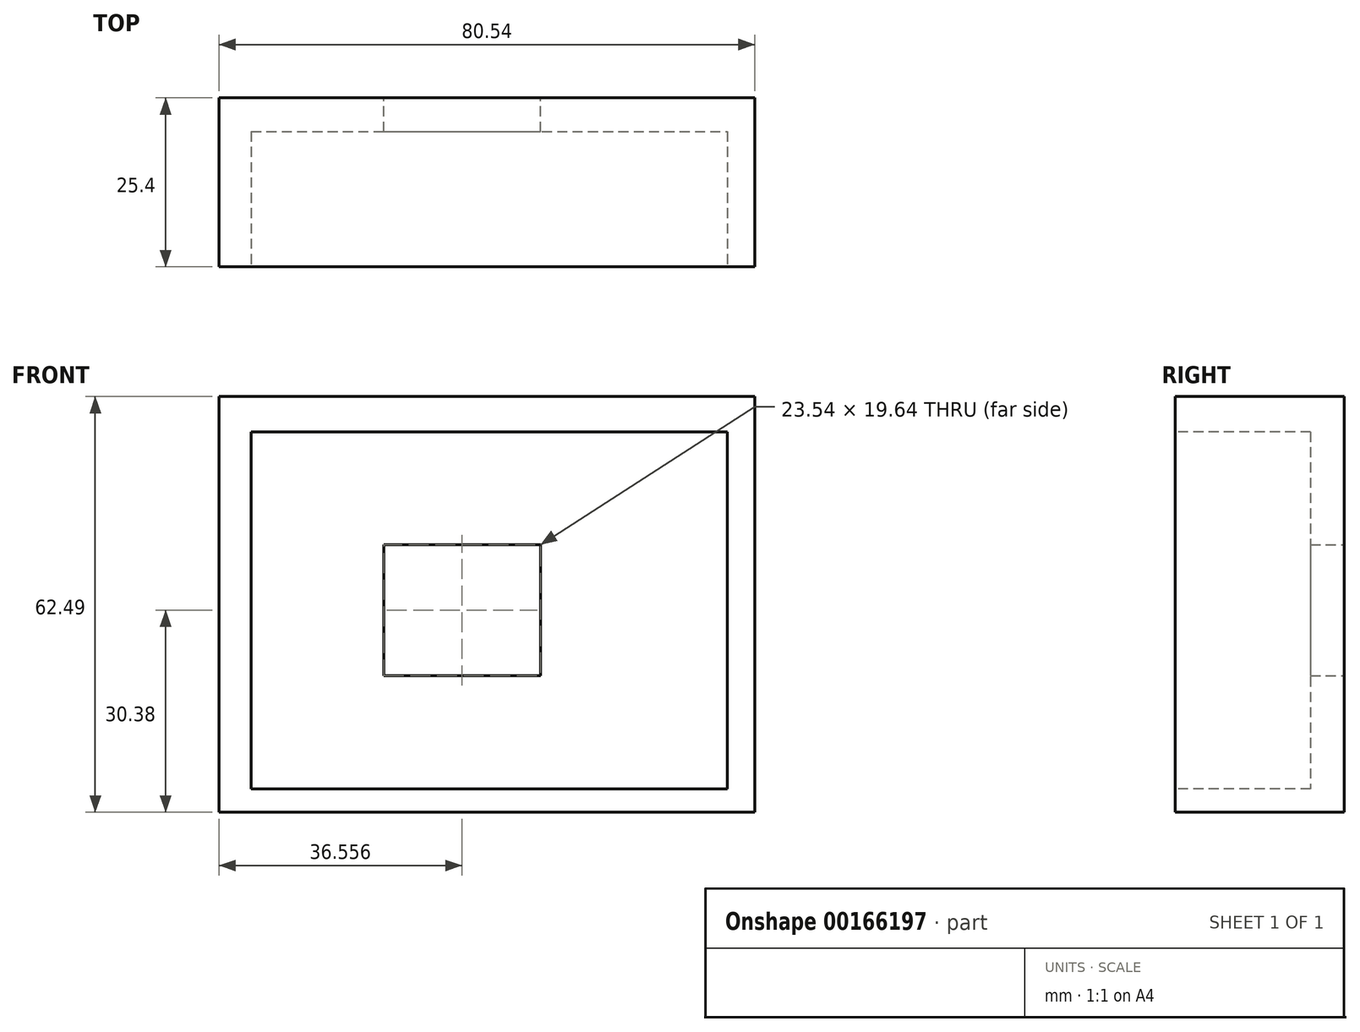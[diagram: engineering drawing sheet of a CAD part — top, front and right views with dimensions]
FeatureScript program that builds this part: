
annotation { "Feature Type Name" : "Feature", "Feature Type Description" : "" }
export const myFeature = defineFeature(function(context is Context, id is Id, definition is map)
    precondition{}
    {
        {
            var Q0;
            Q0=qCreatedBy(makeId("Front.planeOp"),FACE);
            var sketch = newSketch(context, id + "F0", { "sketchPlane" : qUnion([Q0])});
            skLineSegment(sketch, "E0.bottom", {"start": v(-184.2, -7.95) * mm, "end": v(-264.75, -7.95) * mm});
            skLineSegment(sketch, "E0.top", {"start": v(-184.2, -70.44) * mm, "end": v(-264.75, -70.44) * mm});
            skLineSegment(sketch, "E0.left", {"start": v(-184.2, -7.95) * mm, "end": v(-184.2, -70.44) * mm});
            skLineSegment(sketch, "E0.right", {"start": v(-264.75, -7.95) * mm, "end": v(-264.75, -70.44) * mm});
            skLineSegment(sketch, "E1.bottom", {"start": v(-239.97, -30.24) * mm, "end": v(-216.42, -30.24) * mm});
            skLineSegment(sketch, "E1.top", {"start": v(-239.97, -49.88) * mm, "end": v(-216.42, -49.88) * mm});
            skLineSegment(sketch, "E1.left", {"start": v(-239.97, -30.24) * mm, "end": v(-239.97, -49.88) * mm});
            skLineSegment(sketch, "E1.right", {"start": v(-216.42, -30.24) * mm, "end": v(-216.42, -49.88) * mm});
            skSolve(sketch);
        }
        {
            var Q0;
            Q0=makeQuery(id+"F0.imprint","IMPRINT",FACE,{"disambiguationData":[TD([[makeQuery(id+"F0.imprint","IMPRINT",EDGE,{"derivedFrom":sQuery(id+"F0.wireOp",EDGE,"E0.bottom")}),1.0]])]});
            extrude(context, id + "F1", {"entities" : qUnion([Q0]), "depth" : 25.4 * mm});
        }
        {
            var Q0;
            Q0=makeQuery(id+"F1.opExtrude","CAP_FACE",FACE,{"disambiguationData":[OSD([sQuery(id+"F0.wireOp",EDGE,"E0.bottom"),sQuery(id+"F0.wireOp",EDGE,"E0.top"),sQuery(id+"F0.wireOp",EDGE,"E0.left"),sQuery(id+"F0.wireOp",EDGE,"E0.right"),sQuery(id+"F0.wireOp",EDGE,"E1.bottom"),sQuery(id+"F0.wireOp",EDGE,"E1.top"),sQuery(id+"F0.wireOp",EDGE,"E1.left"),sQuery(id+"F0.wireOp",EDGE,"E1.right")])],"isStart":false});
            var sketch = newSketch(context, id + "F2", { "sketchPlane" : qUnion([Q0])});
            skLineSegment(sketch, "E2.bottom", {"start": v(-259.89, -13.26) * mm, "end": v(-188.35, -13.26) * mm});
            skLineSegment(sketch, "E2.top", {"start": v(-259.89, -66.91) * mm, "end": v(-188.35, -66.91) * mm});
            skLineSegment(sketch, "E2.left", {"start": v(-259.89, -13.26) * mm, "end": v(-259.89, -66.91) * mm});
            skLineSegment(sketch, "E2.right", {"start": v(-188.35, -13.26) * mm, "end": v(-188.35, -66.91) * mm});
            skSolve(sketch);
        }
        {
            var Q0;
            Q0 = qSketchRegion(id + "F2", true);
            extrude(context, id + "F3", {"entities" : qUnion([Q0]), "operationType" : NewBodyOperationType.REMOVE, "oppositeDirection" : true, "depth" : 20.32 * mm});
        }
    });
